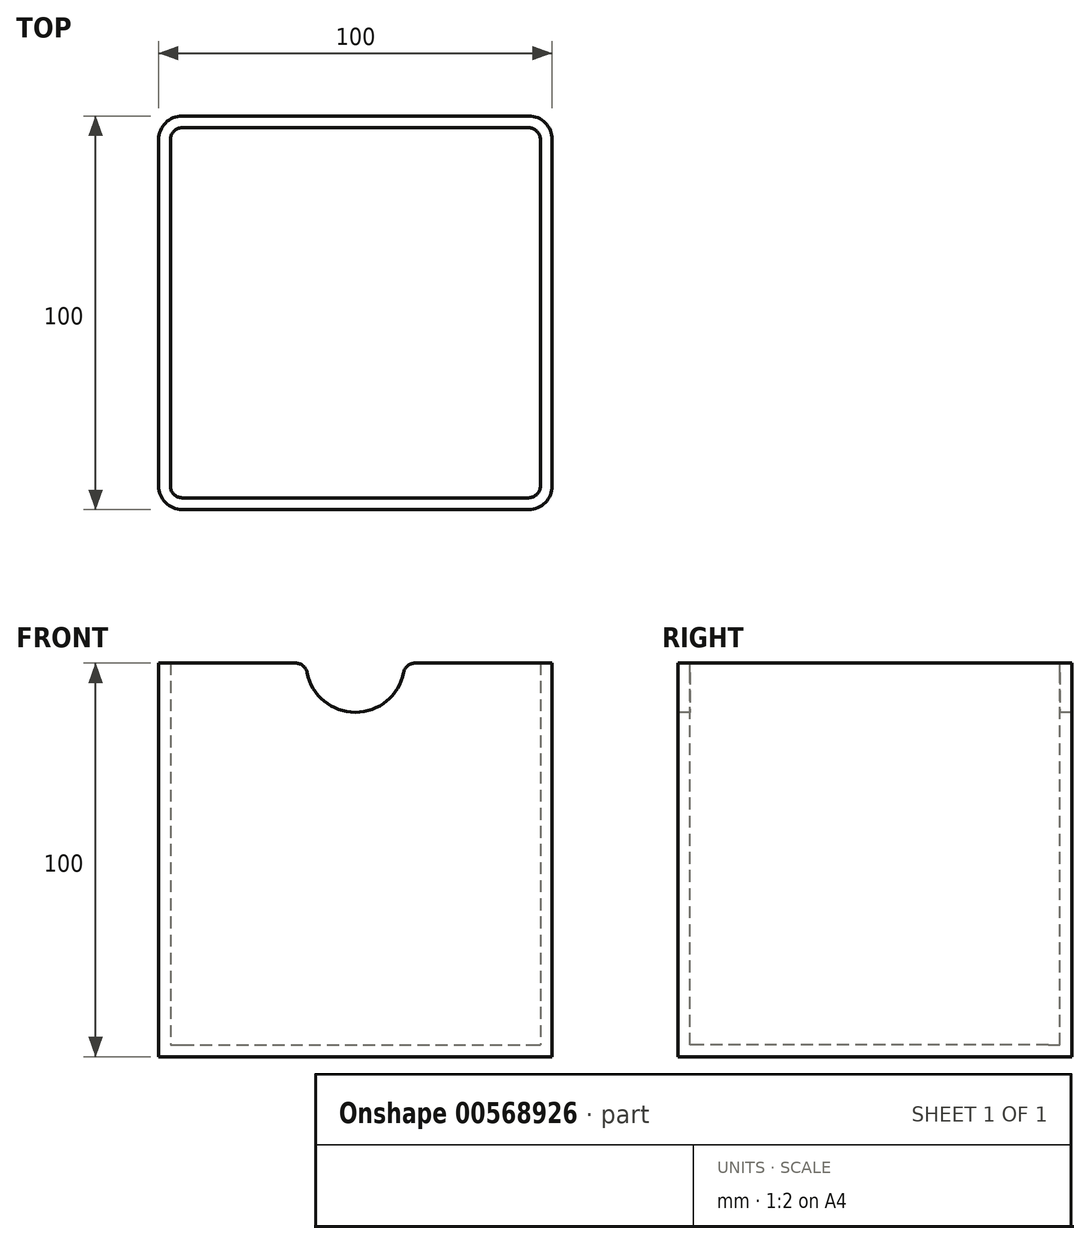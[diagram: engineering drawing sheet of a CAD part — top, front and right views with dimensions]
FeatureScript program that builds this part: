
annotation { "Feature Type Name" : "Feature", "Feature Type Description" : "" }
export const myFeature = defineFeature(function(context is Context, id is Id, definition is map)
    precondition{}
    {
        {
            var Q0;
            Q0=qCreatedBy(makeId("Top.planeOp"),FACE);
            var sketch = newSketch(context, id + "F0", { "sketchPlane" : qUnion([Q0])});
            skLineSegment(sketch, "E0.bottom", {"start": v(-50, 50) * mm, "end": v(50, 50) * mm});
            skLineSegment(sketch, "E0.top", {"start": v(-50, -50) * mm, "end": v(50, -50) * mm});
            skLineSegment(sketch, "E0.left", {"start": v(-50, 50) * mm, "end": v(-50, -50) * mm});
            skLineSegment(sketch, "E0.right", {"start": v(50, 50) * mm, "end": v(50, -50) * mm});
            skPoint(sketch, "E0.middle", {"position": v(0, 0) * mm});
            skSolve(sketch);
        }
        {
            var Q0;
            Q0 = qSketchRegion(id + "F0", true);
            extrude(context, id + "F1", {"entities" : qUnion([Q0]), "depth" : 100 * mm, "offsetDistance" : 25.4 * mm});
        }
        {
            var Q0;
            Q0=makeQuery(id+"F1.opExtrude","SWEPT_EDGE",EDGE,{"disambiguationData":[OSD([sQuery(id+"F0.wireOp",EDGE,"E0.top"),sQuery(id+"F0.wireOp",EDGE,"E0.right")])]});
            var Q1;
            Q1=makeQuery(id+"F1.opExtrude","SWEPT_EDGE",EDGE,{"disambiguationData":[OSD([sQuery(id+"F0.wireOp",EDGE,"E0.top"),sQuery(id+"F0.wireOp",EDGE,"E0.left")])]});
            var Q2;
            Q2=makeQuery(id+"F1.opExtrude","SWEPT_EDGE",EDGE,{"disambiguationData":[OSD([sQuery(id+"F0.wireOp",EDGE,"E0.bottom"),sQuery(id+"F0.wireOp",EDGE,"E0.right")])]});
            var Q3;
            Q3=makeQuery(id+"F1.opExtrude","SWEPT_EDGE",EDGE,{"disambiguationData":[OSD([sQuery(id+"F0.wireOp",EDGE,"E0.bottom"),sQuery(id+"F0.wireOp",EDGE,"E0.left")])]});
            fillet(context, id + "F2", {"entities" : qUnion([Q0, Q1, Q2, Q3]), "radius" : 6 * mm, "tangentPropagation" : true, "allowEdgeOverflow" : false});
        }
        {
            var Q0;
            Q0=makeQuery(id+"F1.opExtrude","CAP_FACE",FACE,{"disambiguationData":[OSD([sQuery(id+"F0.wireOp",EDGE,"E0.bottom"),sQuery(id+"F0.wireOp",EDGE,"E0.top"),sQuery(id+"F0.wireOp",EDGE,"E0.left"),sQuery(id+"F0.wireOp",EDGE,"E0.right")])],"isStart":false});
            shell(context, id + "F3", {"entities" : qUnion([Q0]), "thickness" : 3 * mm});
        }
        {
            var Q0;
            Q0=makeQuery(id+"F1.opExtrude","SWEPT_FACE",FACE,{"disambiguationData":[OSD([sQuery(id+"F0.wireOp",EDGE,"E0.top")])]});
            var sketch = newSketch(context, id + "F4", { "sketchPlane" : qUnion([Q0])});
            skCircle(sketch, "E1", {"center": v(0, 100) * mm, "radius": 12.5 * mm});
            skSolve(sketch);
        }
        {
            var Q0;
            Q0 = qSketchRegion(id + "F4", true);
            extrude(context, id + "F5", {"entities" : qUnion([Q0]), "operationType" : NewBodyOperationType.REMOVE, "endBound" : BoundingType.THROUGH_ALL, "oppositeDirection" : true, "depth" : 25.4 * mm, "offsetDistance" : 25.4 * mm});
        }
        {
            var Q0;
            Q0=makeQuery(id+"F5.boolean.opBoolean","INTERSECT",EDGE,{"disambiguationData":[OD(0.0)],"derivedFrom":[makeQuery(id+"F1.opExtrude","CAP_FACE",FACE,{"disambiguationData":[OSD([sQuery(id+"F0.wireOp",EDGE,"E0.bottom"),sQuery(id+"F0.wireOp",EDGE,"E0.top"),sQuery(id+"F0.wireOp",EDGE,"E0.left"),sQuery(id+"F0.wireOp",EDGE,"E0.right")])],"isStart":false}),makeQuery(id+"F5.opExtrude","SWEPT_FACE",FACE,{"disambiguationData":[OSD([sQuery(id+"F4.wireOp",EDGE,"E1")])]})]});
            var Q1;
            Q1=makeQuery(id+"F5.boolean.opBoolean","INTERSECT",EDGE,{"disambiguationData":[OD(1.0)],"derivedFrom":[makeQuery(id+"F1.opExtrude","CAP_FACE",FACE,{"disambiguationData":[OSD([sQuery(id+"F0.wireOp",EDGE,"E0.bottom"),sQuery(id+"F0.wireOp",EDGE,"E0.top"),sQuery(id+"F0.wireOp",EDGE,"E0.left"),sQuery(id+"F0.wireOp",EDGE,"E0.right")])],"isStart":false}),makeQuery(id+"F5.opExtrude","SWEPT_FACE",FACE,{"disambiguationData":[OSD([sQuery(id+"F4.wireOp",EDGE,"E1")])]})]});
            var Q2;
            Q2=makeQuery(id+"F5.boolean.opBoolean","INTERSECT",EDGE,{"disambiguationData":[OD(2.0)],"derivedFrom":[makeQuery(id+"F1.opExtrude","CAP_FACE",FACE,{"disambiguationData":[OSD([sQuery(id+"F0.wireOp",EDGE,"E0.bottom"),sQuery(id+"F0.wireOp",EDGE,"E0.top"),sQuery(id+"F0.wireOp",EDGE,"E0.left"),sQuery(id+"F0.wireOp",EDGE,"E0.right")])],"isStart":false}),makeQuery(id+"F5.opExtrude","SWEPT_FACE",FACE,{"disambiguationData":[OSD([sQuery(id+"F4.wireOp",EDGE,"E1")])]})]});
            var Q3;
            Q3=makeQuery(id+"F5.boolean.opBoolean","INTERSECT",EDGE,{"disambiguationData":[OD(3.0)],"derivedFrom":[makeQuery(id+"F1.opExtrude","CAP_FACE",FACE,{"disambiguationData":[OSD([sQuery(id+"F0.wireOp",EDGE,"E0.bottom"),sQuery(id+"F0.wireOp",EDGE,"E0.top"),sQuery(id+"F0.wireOp",EDGE,"E0.left"),sQuery(id+"F0.wireOp",EDGE,"E0.right")])],"isStart":false}),makeQuery(id+"F5.opExtrude","SWEPT_FACE",FACE,{"disambiguationData":[OSD([sQuery(id+"F4.wireOp",EDGE,"E1")])]})]});
            fillet(context, id + "F6", {"entities" : qUnion([Q0, Q1, Q2, Q3]), "radius" : 3 * mm, "tangentPropagation" : true, "allowEdgeOverflow" : false});
        }
    });
